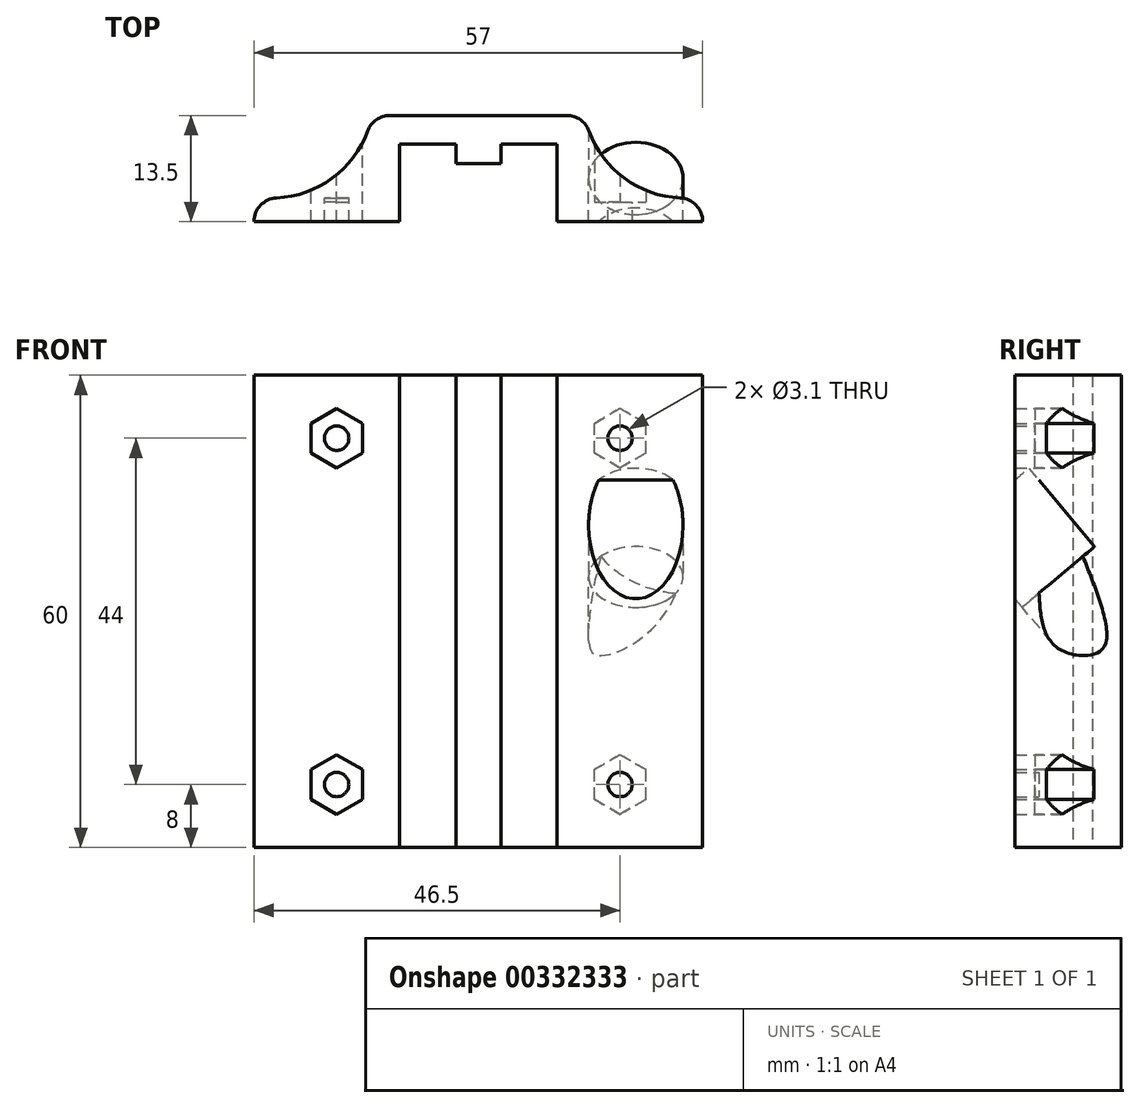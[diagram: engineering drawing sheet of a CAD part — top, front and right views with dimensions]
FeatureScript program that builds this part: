
annotation { "Feature Type Name" : "Feature", "Feature Type Description" : "" }
export const myFeature = defineFeature(function(context is Context, id is Id, definition is map)
    precondition{}
    {
        {
            var Q0;
            Q0=qCreatedBy(makeId("Top.planeOp"),FACE);
            var sketch = newSketch(context, id + "F0", { "sketchPlane" : qUnion([Q0])});
            skLineSegment(sketch, "E0.bottom", {"start": v(10, -9.85) * mm, "end": v(-10, -9.85) * mm});
            skLineSegment(sketch, "E0.top", {"start": v(10, 9.85) * mm, "end": v(-10, 9.85) * mm});
            skLineSegment(sketch, "E0.left", {"start": v(10, -9.85) * mm, "end": v(10, 9.85) * mm});
            skLineSegment(sketch, "E0.right", {"start": v(-10, -9.85) * mm, "end": v(-10, 9.85) * mm});
            skPoint(sketch, "E0.middle", {"position": v(0, 0) * mm});
            skLineSegment(sketch, "E1.left", {"start": v(2.85, 9.85) * mm, "end": v(2.85, 7.35) * mm});
            skLineSegment(sketch, "E1.right", {"start": v(-2.85, 9.85) * mm, "end": v(-2.85, 7.35) * mm});
            skLineSegment(sketch, "E2.bottom", {"start": v(10, -3) * mm, "end": v(6, -3) * mm});
            skLineSegment(sketch, "E2.top", {"start": v(10, 3) * mm, "end": v(6, 3) * mm});
            skLineSegment(sketch, "E3.0", {"start": v(2.85, 7.35) * mm, "end": v(-2.85, 7.35) * mm});
            skLineSegment(sketch, "E4.0", {"start": v(6, -3) * mm, "end": v(6, 3) * mm});
            skLineSegment(sketch, "E5.MirrorCS", {"start": v(-10, 3) * mm, "end": v(-6, 3) * mm});
            skLineSegment(sketch, "E6.MirrorCS", {"start": v(-6, -3) * mm, "end": v(-6, 3) * mm});
            skLineSegment(sketch, "E7.MirrorCS", {"start": v(-10, -3) * mm, "end": v(-6, -3) * mm});
            skLineSegment(sketch, "E8.MirrorCS", {"start": v(-2.85, -9.85) * mm, "end": v(-2.85, -7.35) * mm});
            skLineSegment(sketch, "E9.MirrorCS", {"start": v(2.85, -7.35) * mm, "end": v(-2.85, -7.35) * mm});
            skLineSegment(sketch, "E10.MirrorCS", {"start": v(2.85, -9.85) * mm, "end": v(2.85, -7.35) * mm});
            skLineSegment(sketch, "E11.bottom", {"start": v(13.5, -13.5) * mm, "end": v(-13.5, -13.5) * mm});
            skLineSegment(sketch, "E11.top", {"start": v(13.5, 13.5) * mm, "end": v(-13.5, 13.5) * mm});
            skLineSegment(sketch, "E11.left", {"start": v(13.5, -13.5) * mm, "end": v(13.5, 13.5) * mm});
            skLineSegment(sketch, "E11.right", {"start": v(-13.5, -13.5) * mm, "end": v(-13.5, 13.5) * mm});
            skLineSegment(sketch, "E12.bottom", {"start": v(28.5, -3) * mm, "end": v(13.5, -3) * mm});
            skLineSegment(sketch, "E12.top", {"start": v(28.5, 3) * mm, "end": v(13.5, 3) * mm});
            skLineSegment(sketch, "E12.left", {"start": v(28.5, -3) * mm, "end": v(28.5, 3) * mm});
            skLineSegment(sketch, "E12.right", {"start": v(13.5, -3) * mm, "end": v(13.5, 3) * mm});
            skPoint(sketch, "E12.middle", {"position": v(21, 0) * mm});
            skLineSegment(sketch, "E13.MirrorCS", {"start": v(-28.5, 3) * mm, "end": v(-13.5, 3) * mm});
            skLineSegment(sketch, "E14.MirrorCS", {"start": v(-28.5, -3) * mm, "end": v(-28.5, 3) * mm});
            skLineSegment(sketch, "E15.MirrorCS", {"start": v(-28.5, -3) * mm, "end": v(-13.5, -3) * mm});
            skLineSegment(sketch, "E16", {"start": v(-28.5, 0) * mm, "end": v(28.5, 0) * mm});
            skSolve(sketch);
        }
        {
            var Q0;
            {var subQ0=sQuery(id+"F0.wireOp",EDGE,"E13.MirrorCS");Q0=makeQuery(id+"F0.imprint","IMPRINT",FACE,{"disambiguationData":[TD([[makeQuery(id+"F0.imprint","IMPRINT",EDGE,{"derivedFrom":subQ0}),-1.0]])]});}
            var Q1;
            {var subQ0=sQuery(id+"F0.wireOp",EDGE,"E11.top");Q1=makeQuery(id+"F0.imprint","IMPRINT",FACE,{"disambiguationData":[TD([[makeQuery(id+"F0.imprint","IMPRINT",EDGE,{"derivedFrom":subQ0}),1.0]])]});}
            var Q2;
            {var subQ0=sQuery(id+"F0.wireOp",EDGE,"E1.left");Q2=makeQuery(id+"F0.imprint","IMPRINT",FACE,{"disambiguationData":[TD([[makeQuery(id+"F0.imprint","IMPRINT",EDGE,{"derivedFrom":subQ0}),-1.0]])]});}
            var Q3;
            {var subQ0=sQuery(id+"F0.wireOp",EDGE,"E12.top");Q3=makeQuery(id+"F0.imprint","IMPRINT",FACE,{"disambiguationData":[TD([[makeQuery(id+"F0.imprint","IMPRINT",EDGE,{"derivedFrom":subQ0}),1.0]])]});}
            extrude(context, id + "F1", {"entities" : qUnion([Q0, Q1, Q2, Q3]), "depth" : 60 * mm});
        }
        {
            var Q0;
            {var subQ0=sQuery(id+"F0.wireOp",EDGE,"E15.MirrorCS");Q0=makeQuery(id+"F0.imprint","IMPRINT",FACE,{"disambiguationData":[TD([[makeQuery(id+"F0.imprint","IMPRINT",EDGE,{"derivedFrom":subQ0}),1.0]])]});}
            var Q1;
            {var subQ1=sQuery(id+"F0.wireOp",EDGE,"E11.bottom");Q1=makeQuery(id+"F0.imprint","IMPRINT",FACE,{"disambiguationData":[TD([[makeQuery(id+"F0.imprint","IMPRINT",EDGE,{"derivedFrom":subQ1}),-1.0]])]});}
            var Q2;
            {var subQ0=sQuery(id+"F0.wireOp",EDGE,"E8.MirrorCS");Q2=makeQuery(id+"F0.imprint","IMPRINT",FACE,{"disambiguationData":[TD([[makeQuery(id+"F0.imprint","IMPRINT",EDGE,{"derivedFrom":subQ0}),-1.0]])]});}
            var Q3;
            {var subQ0=sQuery(id+"F0.wireOp",EDGE,"E12.bottom");Q3=makeQuery(id+"F0.imprint","IMPRINT",FACE,{"disambiguationData":[TD([[makeQuery(id+"F0.imprint","IMPRINT",EDGE,{"derivedFrom":subQ0}),-1.0]])]});}
            extrude(context, id + "F2", {"entities" : qUnion([Q0, Q1, Q2, Q3]), "depth" : 60 * mm});
        }
        {
            var Q0;
            Q0=qCreatedBy(makeId("Front.planeOp"),FACE);
            var sketch = newSketch(context, id + "F3", { "sketchPlane" : qUnion([Q0])});
            skCircle(sketch, "E17", {"center": v(18, 52) * mm, "radius": 1.55 * mm});
            skCircle(sketch, "E18", {"center": v(18, 8) * mm, "radius": 1.55 * mm});
            skCircle(sketch, "E19.cCircle", {"center": v(18, 52) * mm, "radius": 3.28 * mm, "construction": true});
            skLineSegment(sketch, "E19.0", {"start": v(21.27, 53.9) * mm, "end": v(21.27, 50.1) * mm});
            skLineSegment(sketch, "E19.1", {"start": v(21.27, 50.1) * mm, "end": v(18, 48.22) * mm});
            skLineSegment(sketch, "E19.2", {"start": v(18, 48.22) * mm, "end": v(14.72, 50.1) * mm});
            skLineSegment(sketch, "E19.3", {"start": v(14.72, 50.1) * mm, "end": v(14.72, 53.9) * mm});
            skLineSegment(sketch, "E19.4", {"start": v(14.72, 53.9) * mm, "end": v(18, 55.78) * mm});
            skLineSegment(sketch, "E19.5", {"start": v(18, 55.78) * mm, "end": v(21.27, 53.9) * mm});
            skPoint(sketch, "E19.0.midPoint", {"position": v(21.27, 52) * mm});
            skCircle(sketch, "E20.cCircle", {"center": v(18, 8) * mm, "radius": 3.28 * mm, "construction": true});
            skLineSegment(sketch, "E20.0", {"start": v(21.28, 9.9) * mm, "end": v(21.28, 6.1) * mm});
            skLineSegment(sketch, "E20.1", {"start": v(21.28, 6.1) * mm, "end": v(18, 4.22) * mm});
            skLineSegment(sketch, "E20.2", {"start": v(18, 4.22) * mm, "end": v(14.73, 6.1) * mm});
            skLineSegment(sketch, "E20.3", {"start": v(14.73, 6.1) * mm, "end": v(14.73, 9.9) * mm});
            skLineSegment(sketch, "E20.4", {"start": v(14.73, 9.9) * mm, "end": v(18, 11.78) * mm});
            skLineSegment(sketch, "E20.5", {"start": v(18, 11.78) * mm, "end": v(21.28, 9.9) * mm});
            skPoint(sketch, "E20.0.midPoint", {"position": v(21.28, 8) * mm});
            skPoint(sketch, "E21.MirrorP", {"position": v(-21.27, 52) * mm});
            skCircle(sketch, "E22.MirrorC", {"center": v(-18, 52) * mm, "radius": 1.55 * mm});
            skLineSegment(sketch, "E23.MirrorCS", {"start": v(-18, 55.78) * mm, "end": v(-21.27, 53.9) * mm});
            skLineSegment(sketch, "E24.MirrorCS", {"start": v(-14.72, 53.9) * mm, "end": v(-18, 55.78) * mm});
            skLineSegment(sketch, "E25.MirrorCS", {"start": v(-14.72, 50.1) * mm, "end": v(-14.72, 53.9) * mm});
            skLineSegment(sketch, "E26.MirrorCS", {"start": v(-18, 48.22) * mm, "end": v(-14.72, 50.1) * mm});
            skLineSegment(sketch, "E27.MirrorCS", {"start": v(-21.27, 50.1) * mm, "end": v(-18, 48.22) * mm});
            skCircle(sketch, "E28.MirrorC", {"center": v(-18, 52) * mm, "radius": 3.28 * mm, "construction": true});
            skLineSegment(sketch, "E29.MirrorCS", {"start": v(-21.27, 53.9) * mm, "end": v(-21.27, 50.1) * mm});
            skLineSegment(sketch, "E30.MirrorCS", {"start": v(-21.28, 9.9) * mm, "end": v(-21.28, 6.1) * mm});
            skLineSegment(sketch, "E31.MirrorCS", {"start": v(-18, 11.78) * mm, "end": v(-21.28, 9.9) * mm});
            skPoint(sketch, "E32.MirrorP", {"position": v(-21.28, 8) * mm});
            skLineSegment(sketch, "E33.MirrorCS", {"start": v(-14.73, 9.9) * mm, "end": v(-18, 11.78) * mm});
            skLineSegment(sketch, "E34.MirrorCS", {"start": v(-14.73, 6.1) * mm, "end": v(-14.73, 9.9) * mm});
            skCircle(sketch, "E35.MirrorC", {"center": v(-18, 8) * mm, "radius": 1.55 * mm});
            skCircle(sketch, "E36.MirrorC", {"center": v(-18, 8) * mm, "radius": 3.28 * mm, "construction": true});
            skLineSegment(sketch, "E37.MirrorCS", {"start": v(-18, 4.22) * mm, "end": v(-14.73, 6.1) * mm});
            skLineSegment(sketch, "E38.MirrorCS", {"start": v(-21.28, 6.1) * mm, "end": v(-18, 4.22) * mm});
            skSolve(sketch);
        }
        {
            var Q0;
            Q0=makeQuery(id+"F3.imprint","IMPRINT",FACE,{"disambiguationData":[TD([[makeQuery(id+"F3.imprint","IMPRINT",EDGE,{"derivedFrom":sQuery(id+"F3.wireOp",EDGE,"E17")}),1.0]])]});
            var Q1;
            Q1=makeQuery(id+"F3.imprint","IMPRINT",FACE,{"disambiguationData":[TD([[makeQuery(id+"F3.imprint","IMPRINT",EDGE,{"derivedFrom":sQuery(id+"F3.wireOp",EDGE,"E22.MirrorC")}),-1.0]])]});
            var Q2;
            Q2=makeQuery(id+"F3.imprint","IMPRINT",FACE,{"disambiguationData":[TD([[makeQuery(id+"F3.imprint","IMPRINT",EDGE,{"derivedFrom":sQuery(id+"F3.wireOp",EDGE,"E35.MirrorC")}),-1.0]])]});
            var Q3;
            Q3=makeQuery(id+"F3.imprint","IMPRINT",FACE,{"disambiguationData":[TD([[makeQuery(id+"F3.imprint","IMPRINT",EDGE,{"derivedFrom":sQuery(id+"F3.wireOp",EDGE,"E18")}),1.0]])]});
            extrude(context, id + "F4", {"entities" : qUnion([Q0, Q1, Q2, Q3]), "operationType" : NewBodyOperationType.REMOVE, "depth" : 10 * mm, "hasSecondDirection" : true, "secondDirectionOppositeDirection" : true, "secondDirectionDepth" : 10 * mm});
        }
        {
            var Q0;
            Q0=makeQuery(id+"F1.opExtrude","SWEPT_EDGE",EDGE,{"disambiguationData":[OSD([sQuery(id+"F0.wireOp",EDGE,"E11.left"),sQuery(id+"F0.wireOp",EDGE,"E12.top"),sQuery(id+"F0.wireOp",EDGE,"E12.right")])]});
            var Q1;
            Q1=makeQuery(id+"F1.opExtrude","SWEPT_EDGE",EDGE,{"disambiguationData":[OSD([sQuery(id+"F0.wireOp",EDGE,"E11.right"),sQuery(id+"F0.wireOp",EDGE,"E13.MirrorCS")])]});
            var Q2;
            Q2=makeQuery(id+"F2.opExtrude","SWEPT_EDGE",EDGE,{"disambiguationData":[OSD([sQuery(id+"F0.wireOp",EDGE,"E11.right"),sQuery(id+"F0.wireOp",EDGE,"E15.MirrorCS")])]});
            var Q3;
            Q3=makeQuery(id+"F2.opExtrude","SWEPT_EDGE",EDGE,{"disambiguationData":[OSD([sQuery(id+"F0.wireOp",EDGE,"E11.left"),sQuery(id+"F0.wireOp",EDGE,"E12.bottom"),sQuery(id+"F0.wireOp",EDGE,"E12.right")])]});
            fillet(context, id + "F5", {"entities" : qUnion([Q0, Q1, Q2, Q3]), "radius" : 13 * mm, "tangentPropagation" : true, "allowEdgeOverflow" : false});
        }
        {
            var Q0;
            Q0=qCreatedBy(makeId("Front.planeOp"),FACE);
            var sketch = newSketch(context, id + "F6", { "sketchPlane" : qUnion([Q0])});
            skCircle(sketch, "E39", {"center": v(18, 52) * mm, "radius": 2.6 * mm});
            skCircle(sketch, "E40", {"center": v(18, 8) * mm, "radius": 2.6 * mm});
            skCircle(sketch, "E41", {"center": v(-18, 52) * mm, "radius": 2.6 * mm});
            skCircle(sketch, "E42", {"center": v(-18, 8) * mm, "radius": 2.6 * mm});
            skSolve(sketch);
        }
        {
            var Q0;
            Q0=makeQuery(id+"F6.imprint","IMPRINT",FACE,{"disambiguationData":[TD([[makeQuery(id+"F6.imprint","IMPRINT",EDGE,{"derivedFrom":sQuery(id+"F6.wireOp",EDGE,"E39")}),1.0]])]});
            var Q1;
            Q1=makeQuery(id+"F3.imprint","IMPRINT",FACE,{"disambiguationData":[TD([[makeQuery(id+"F3.imprint","IMPRINT",EDGE,{"derivedFrom":sQuery(id+"F3.wireOp",EDGE,"E17")}),1.0]])]});
            var Q2;
            Q2=makeQuery(id+"F6.imprint","IMPRINT",FACE,{"disambiguationData":[TD([[makeQuery(id+"F6.imprint","IMPRINT",EDGE,{"derivedFrom":sQuery(id+"F6.wireOp",EDGE,"E40")}),1.0]])]});
            var Q3;
            Q3=makeQuery(id+"F3.imprint","IMPRINT",FACE,{"disambiguationData":[TD([[makeQuery(id+"F3.imprint","IMPRINT",EDGE,{"derivedFrom":sQuery(id+"F3.wireOp",EDGE,"E18")}),1.0]])]});
            var Q4;
            Q4=makeQuery(id+"F6.imprint","IMPRINT",FACE,{"disambiguationData":[TD([[makeQuery(id+"F6.imprint","IMPRINT",EDGE,{"derivedFrom":sQuery(id+"F6.wireOp",EDGE,"E42")}),1.0]])]});
            var Q5;
            Q5=makeQuery(id+"F3.imprint","IMPRINT",FACE,{"disambiguationData":[TD([[makeQuery(id+"F3.imprint","IMPRINT",EDGE,{"derivedFrom":sQuery(id+"F3.wireOp",EDGE,"E35.MirrorC")}),-1.0]])]});
            var Q6;
            Q6=makeQuery(id+"F6.imprint","IMPRINT",FACE,{"disambiguationData":[TD([[makeQuery(id+"F6.imprint","IMPRINT",EDGE,{"derivedFrom":sQuery(id+"F6.wireOp",EDGE,"E41")}),1.0]])]});
            var Q7;
            Q7=makeQuery(id+"F3.imprint","IMPRINT",FACE,{"disambiguationData":[TD([[makeQuery(id+"F3.imprint","IMPRINT",EDGE,{"derivedFrom":sQuery(id+"F3.wireOp",EDGE,"E22.MirrorC")}),-1.0]])]});
            extrude(context, id + "F7", {"entities" : qUnion([Q0, Q1, Q2, Q3, Q4, Q5, Q6, Q7]), "operationType" : NewBodyOperationType.REMOVE, "depth" : 25 * mm, "hasSecondDirection" : true, "secondDirectionOppositeDirection" : false, "secondDirectionDepth" : 3 * mm});
        }
        {
            var Q0;
            {var subQ3=sQuery(id+"F0.wireOp",EDGE,"E1.left");Q0=makeQuery(id+"F0.imprint","IMPRINT",FACE,{"disambiguationData":[TD([[makeQuery(id+"F0.imprint","IMPRINT",EDGE,{"derivedFrom":subQ3}),1.0]])]});}
            var Q1;
            {var subQ0=sQuery(id+"F0.wireOp",EDGE,"E2.top");Q1=makeQuery(id+"F0.imprint","IMPRINT",FACE,{"disambiguationData":[TD([[makeQuery(id+"F0.imprint","IMPRINT",EDGE,{"derivedFrom":subQ0}),1.0]])]});}
            var Q2;
            {var subQ0=sQuery(id+"F0.wireOp",EDGE,"E5.MirrorCS");Q2=makeQuery(id+"F0.imprint","IMPRINT",FACE,{"disambiguationData":[TD([[makeQuery(id+"F0.imprint","IMPRINT",EDGE,{"derivedFrom":subQ0}),-1.0]])]});}
            extrude(context, id + "F8", {"entities" : qUnion([Q0, Q1, Q2]), "operationType" : NewBodyOperationType.REMOVE, "depth" : 40 * mm});
        }
        {
            var Q0;
            Q0=makeQuery(id+"F5.opFillet","BLEND_EDGE",EDGE,{"blendedFrom":[makeQuery(id+"F2.opExtrude","SWEPT_EDGE",EDGE,{"disambiguationData":[OSD([sQuery(id+"F0.wireOp",EDGE,"E11.left"),sQuery(id+"F0.wireOp",EDGE,"E12.bottom"),sQuery(id+"F0.wireOp",EDGE,"E12.right")])]}),makeQuery(id+"F2.opExtrude","SWEPT_FACE",FACE,{"disambiguationData":[OSD([sQuery(id+"F0.wireOp",EDGE,"E11.bottom")])]})],"blendedInto":[makeQuery(id+"F2.opExtrude","SWEPT_FACE",FACE,{"disambiguationData":[OSD([sQuery(id+"F0.wireOp",EDGE,"E11.bottom")])]})]});
            var Q1;
            Q1=makeQuery(id+"F5.opFillet","BLEND_EDGE",EDGE,{"blendedFrom":[makeQuery(id+"F2.opExtrude","SWEPT_EDGE",EDGE,{"disambiguationData":[OSD([sQuery(id+"F0.wireOp",EDGE,"E11.right"),sQuery(id+"F0.wireOp",EDGE,"E15.MirrorCS")])]}),makeQuery(id+"F2.opExtrude","SWEPT_FACE",FACE,{"disambiguationData":[OSD([sQuery(id+"F0.wireOp",EDGE,"E11.bottom")])]})],"blendedInto":[makeQuery(id+"F2.opExtrude","SWEPT_FACE",FACE,{"disambiguationData":[OSD([sQuery(id+"F0.wireOp",EDGE,"E11.bottom")])]})]});
            var Q2;
            Q2=makeQuery(id+"F5.opFillet","BLEND_EDGE",EDGE,{"blendedFrom":[makeQuery(id+"F1.opExtrude","SWEPT_EDGE",EDGE,{"disambiguationData":[OSD([sQuery(id+"F0.wireOp",EDGE,"E11.left"),sQuery(id+"F0.wireOp",EDGE,"E12.top"),sQuery(id+"F0.wireOp",EDGE,"E12.right")])]}),makeQuery(id+"F1.opExtrude","SWEPT_FACE",FACE,{"disambiguationData":[OSD([sQuery(id+"F0.wireOp",EDGE,"E11.top")])]})],"blendedInto":[makeQuery(id+"F1.opExtrude","SWEPT_FACE",FACE,{"disambiguationData":[OSD([sQuery(id+"F0.wireOp",EDGE,"E11.top")])]})]});
            var Q3;
            Q3=makeQuery(id+"F5.opFillet","BLEND_EDGE",EDGE,{"blendedFrom":[makeQuery(id+"F1.opExtrude","SWEPT_EDGE",EDGE,{"disambiguationData":[OSD([sQuery(id+"F0.wireOp",EDGE,"E11.right"),sQuery(id+"F0.wireOp",EDGE,"E13.MirrorCS")])]}),makeQuery(id+"F1.opExtrude","SWEPT_FACE",FACE,{"disambiguationData":[OSD([sQuery(id+"F0.wireOp",EDGE,"E11.top")])]})],"blendedInto":[makeQuery(id+"F1.opExtrude","SWEPT_FACE",FACE,{"disambiguationData":[OSD([sQuery(id+"F0.wireOp",EDGE,"E11.top")])]})]});
            fillet(context, id + "F9", {"entities" : qUnion([Q0, Q1, Q2, Q3]), "radius" : 3 * mm, "tangentPropagation" : true, "allowEdgeOverflow" : false});
        }
        {
            var Q0;
            Q0=qCreatedBy(makeId("Front.planeOp"),FACE);
            var sketch = newSketch(context, id + "F10", { "sketchPlane" : qUnion([Q0])});
            skLineSegment(sketch, "E43.bottom", {"start": v(-10, 15) * mm, "end": v(-4, 15) * mm});
            skLineSegment(sketch, "E43.top", {"start": v(-10, 45) * mm, "end": v(-4, 45) * mm});
            skLineSegment(sketch, "E43.left", {"start": v(-10, 15) * mm, "end": v(-10, 45) * mm});
            skLineSegment(sketch, "E43.right", {"start": v(-4, 15) * mm, "end": v(-4, 45) * mm});
            skPoint(sketch, "E43.middle", {"position": v(0, 31.47) * mm});
            skSolve(sketch);
        }
        {
            var Q0;
            Q0=makeQuery(id+"F10.imprint","IMPRINT",FACE,{"disambiguationData":[TD([[makeQuery(id+"F10.imprint","IMPRINT",EDGE,{"derivedFrom":sQuery(id+"F10.wireOp",EDGE,"E43.bottom")}),1.0]])]});
            extrude(context, id + "F11", {"entities" : qUnion([Q0]), "operationType" : NewBodyOperationType.ADD, "depth" : 26 * mm, "hasSecondDirection" : true, "secondDirectionOppositeDirection" : false, "secondDirectionDepth" : 11 * mm});
        }
        {
            var Q0;
            {var subQ1=sQuery(id+"F10.wireOp",EDGE,"E43.left");Q0=makeQuery(id+"F11.boolean.opBoolean","SPLIT",FACE,{"disambiguationData":[TD([makeQuery(id+"FrOpPQLDhbuZp0P_2.opFillet","BLEND_FACE",FACE,{"disambiguationData":[OSD([sQuery(id+"F0.wireOp",EDGE,"E11.bottom"),sQuery(id+"F0.wireOp",EDGE,"E11.right")])]})])],"derivedFrom":makeQuery(id+"F11.opExtrude","SWEPT_FACE",FACE,{"disambiguationData":[OSD([subQ1])]})});}
            cPlane(context, id + "F12", {"entities" : qUnion([Q0]), "cplaneType" : CPlaneType.OFFSET, "offset" : 0 * mm, "width" : 150 * mm, "height" : 150 * mm});
        }
        {
            var Q0;
            Q0=qCreatedBy(id+"F12.planeOp",FACE);
            var sketch = newSketch(context, id + "F13", { "sketchPlane" : qUnion([Q0])});
            skCircle(sketch, "E44", {"center": v(21, 30) * mm, "radius": 1.55 * mm});
            skCircle(sketch, "E45.cCircle", {"center": v(21, 30) * mm, "radius": 3.28 * mm, "construction": true});
            skLineSegment(sketch, "E45.0", {"start": v(24.28, 31.9) * mm, "end": v(24.28, 28.1) * mm});
            skLineSegment(sketch, "E45.1", {"start": v(24.28, 28.1) * mm, "end": v(21, 26.22) * mm});
            skLineSegment(sketch, "E45.2", {"start": v(21, 26.22) * mm, "end": v(17.72, 28.1) * mm});
            skLineSegment(sketch, "E45.3", {"start": v(17.73, 28.1) * mm, "end": v(17.73, 31.9) * mm});
            skLineSegment(sketch, "E45.4", {"start": v(17.73, 31.9) * mm, "end": v(21, 33.78) * mm});
            skLineSegment(sketch, "E45.5", {"start": v(21, 33.78) * mm, "end": v(24.28, 31.9) * mm});
            skPoint(sketch, "E45.0.midPoint", {"position": v(24.28, 30) * mm});
            skSolve(sketch);
        }
        {
            var Q0;
            Q0=makeQuery(id+"F11.boolean.opBoolean","INTERSECT",EDGE,{"derivedFrom":[makeQuery(id+"FrOpPQLDhbuZp0P_2.opFillet","BLEND_FACE",FACE,{"disambiguationData":[OSD([sQuery(id+"F0.wireOp",EDGE,"E11.bottom"),sQuery(id+"F0.wireOp",EDGE,"E11.right")])]}),makeQuery(id+"F11.opExtrude","SWEPT_FACE",FACE,{"disambiguationData":[OSD([sQuery(id+"F10.wireOp",EDGE,"E43.left")])]})]});
            var Q1;
            Q1=makeQuery(id+"F11.boolean.opBoolean","INTERSECT",EDGE,{"derivedFrom":[makeQuery(id+"FrOpPQLDhbuZp0P_2.opFillet","BLEND_FACE",FACE,{"disambiguationData":[OSD([sQuery(id+"F0.wireOp",EDGE,"E11.bottom"),sQuery(id+"F0.wireOp",EDGE,"E11.right")])]}),makeQuery(id+"F11.opExtrude","SWEPT_FACE",FACE,{"disambiguationData":[OSD([sQuery(id+"F10.wireOp",EDGE,"E43.top")])]})]});
            var Q2;
            Q2=makeQuery(id+"F11.boolean.opBoolean","INTERSECT",EDGE,{"derivedFrom":[makeQuery(id+"FrOpPQLDhbuZp0P_2.opFillet","BLEND_FACE",FACE,{"disambiguationData":[OSD([sQuery(id+"F0.wireOp",EDGE,"E11.bottom"),sQuery(id+"F0.wireOp",EDGE,"E11.right")])]}),makeQuery(id+"F11.opExtrude","SWEPT_FACE",FACE,{"disambiguationData":[OSD([sQuery(id+"F10.wireOp",EDGE,"E43.bottom")])]})]});
            var Q3;
            Q3=makeQuery(id+"F11.boolean.opBoolean","INTERSECT",EDGE,{"derivedFrom":[makeQuery(id+"F2.opExtrude","SWEPT_FACE",FACE,{"disambiguationData":[OSD([sQuery(id+"F0.wireOp",EDGE,"E11.bottom")])]}),makeQuery(id+"F11.opExtrude","SWEPT_FACE",FACE,{"disambiguationData":[OSD([sQuery(id+"F10.wireOp",EDGE,"E43.right")])]})]});
            fillet(context, id + "F14", {"entities" : qUnion([Q0, Q1, Q2, Q3]), "radius" : 2 * mm, "tangentPropagation" : true, "allowEdgeOverflow" : false});
        }
        {
            var Q0;
            Q0=makeQuery(id+"F11.opExtrude","CAP_EDGE",EDGE,{"disambiguationData":[OSD([sQuery(id+"F10.wireOp",EDGE,"E43.top")])],"isStart":false});
            var Q1;
            Q1=makeQuery(id+"F11.opExtrude","CAP_EDGE",EDGE,{"disambiguationData":[OSD([sQuery(id+"F10.wireOp",EDGE,"E43.bottom")])],"isStart":false});
            fillet(context, id + "F15", {"entities" : qUnion([Q0, Q1]), "radius" : 5 * mm, "tangentPropagation" : true, "allowEdgeOverflow" : false});
        }
        {
            var Q0;
            Q0=makeQuery(id+"F11.opExtrude","CAP_EDGE",EDGE,{"disambiguationData":[OSD([sQuery(id+"F10.wireOp",EDGE,"E43.left")])],"isStart":false});
            var Q1;
            {var subQ0=makeQuery(id+"FrOpPQLDhbuZp0P_2.opFillet","BLEND_FACE",FACE,{"disambiguationData":[OSD([sQuery(id+"F0.wireOp",EDGE,"E11.bottom"),sQuery(id+"F0.wireOp",EDGE,"E11.right")])]});Q1=makeQuery(id+"F14.opFillet","BLEND_EDGE",EDGE,{"disambiguationData":[OD(1.0)],"blendedFrom":[makeQuery(id+"F11.boolean.opBoolean","INTERSECT",EDGE,{"derivedFrom":[subQ0,makeQuery(id+"F11.opExtrude","SWEPT_FACE",FACE,{"disambiguationData":[OSD([sQuery(id+"F10.wireOp",EDGE,"E43.top")])]})]}),makeQuery(id+"F11.boolean.opBoolean","INTERSECT",EDGE,{"derivedFrom":[subQ0,makeQuery(id+"F11.opExtrude","SWEPT_FACE",FACE,{"disambiguationData":[OSD([sQuery(id+"F10.wireOp",EDGE,"E43.left")])]})]})],"blendedInto":[]});}
            var Q2;
            {var subQ0=makeQuery(id+"FrOpPQLDhbuZp0P_2.opFillet","BLEND_FACE",FACE,{"disambiguationData":[OSD([sQuery(id+"F0.wireOp",EDGE,"E11.bottom"),sQuery(id+"F0.wireOp",EDGE,"E11.right")])]});Q2=makeQuery(id+"F14.opFillet","BLEND_EDGE",EDGE,{"disambiguationData":[OD(1.0)],"blendedFrom":[makeQuery(id+"F11.boolean.opBoolean","INTERSECT",EDGE,{"derivedFrom":[subQ0,makeQuery(id+"F11.opExtrude","SWEPT_FACE",FACE,{"disambiguationData":[OSD([sQuery(id+"F10.wireOp",EDGE,"E43.bottom")])]})]}),makeQuery(id+"F11.boolean.opBoolean","INTERSECT",EDGE,{"derivedFrom":[subQ0,makeQuery(id+"F11.opExtrude","SWEPT_FACE",FACE,{"disambiguationData":[OSD([sQuery(id+"F10.wireOp",EDGE,"E43.left")])]})]})],"blendedInto":[]});}
            var Q3;
            Q3=makeQuery(id+"F11.opExtrude","SWEPT_EDGE",EDGE,{"disambiguationData":[OSD([sQuery(id+"F10.wireOp",EDGE,"E43.bottom"),sQuery(id+"F10.wireOp",EDGE,"E43.left")])]});
            fillet(context, id + "F16", {"entities" : qUnion([Q0, Q1, Q2, Q3]), "radius" : 4 * mm, "tangentPropagation" : true, "allowEdgeOverflow" : false});
        }
        {
            var Q0;
            Q0=makeQuery(id+"F13.imprint","IMPRINT",FACE,{"disambiguationData":[TD([[makeQuery(id+"F13.imprint","IMPRINT",EDGE,{"derivedFrom":sQuery(id+"F13.wireOp",EDGE,"E44")}),1.0]])]});
            extrude(context, id + "F17", {"entities" : qUnion([Q0]), "operationType" : NewBodyOperationType.REMOVE, "oppositeDirection" : true, "depth" : 25 * mm});
        }
        {
            var Q0;
            Q0=makeQuery(id+"F13.imprint","IMPRINT",FACE,{"disambiguationData":[TD([[makeQuery(id+"F13.imprint","IMPRINT",EDGE,{"derivedFrom":sQuery(id+"F13.wireOp",EDGE,"E44")}),-1.0]])]});
            extrude(context, id + "F18", {"entities" : qUnion([Q0]), "operationType" : NewBodyOperationType.REMOVE, "oppositeDirection" : true, "depth" : 2.5 * mm});
        }
        {
            var Q0;
            Q0=qCreatedBy(makeId("Front.planeOp"),FACE);
            cPlane(context, id + "F19", {"entities" : qUnion([Q0]), "cplaneType" : CPlaneType.OFFSET, "offset" : 10 * mm, "oppositeDirection" : true, "width" : 150 * mm, "height" : 150 * mm});
        }
        {
            var Q0;
            Q0=qCreatedBy(id+"F19.planeOp",FACE);
            var sketch = newSketch(context, id + "F20", { "sketchPlane" : qUnion([Q0])});
            skPoint(sketch, "E46.middle", {"position": v(0, 30) * mm});
            skCircle(sketch, "E47", {"center": v(20, 30) * mm, "radius": 6 * mm});
            skCircle(sketch, "E48.MirrorC", {"center": v(-20, 30) * mm, "radius": 6 * mm});
            skSolve(sketch);
        }
        {
            var Q0;
            Q0=qCreatedBy(makeId("Right.planeOp"),FACE);
            var sketch = newSketch(context, id + "F21", { "sketchPlane" : qUnion([Q0])});
            skCircle(sketch, "E49", {"center": v(10, 30) * mm, "radius": 3 * mm});
            skSolve(sketch);
        }
        {
            var Q0;
            Q0=makeQuery(id+"F20.imprint","IMPRINT",FACE,{"disambiguationData":[TD([[makeQuery(id+"F20.imprint","IMPRINT",EDGE,{"derivedFrom":sQuery(id+"F20.wireOp",EDGE,"E47")}),1.0]])]});
            var Q1;
            Q1=makeQuery(id+"F20.imprint","IMPRINT",FACE,{"disambiguationData":[TD([[makeQuery(id+"F20.imprint","IMPRINT",EDGE,{"derivedFrom":sQuery(id+"F20.wireOp",EDGE,"E48.MirrorC")}),-1.0]])]});
            extrude(context, id + "F22", {"entities" : qUnion([Q0, Q1]), "depth" : 20 * mm, "hasSecondDirection" : true, "secondDirectionOppositeDirection" : false, "secondDirectionDepth" : 7 * mm});
        }
        {
            var Q0;
            Q0=makeQuery(id+"F22.opExtrude","SWEPT_BODY",BODY,{"disambiguationData":[OSD([sQuery(id+"F20.wireOp",EDGE,"E47")])]});
            var Q1;
            Q1=makeQuery(id+"F22.opExtrude","SWEPT_BODY",BODY,{"disambiguationData":[OSD([sQuery(id+"F20.wireOp",EDGE,"E48.MirrorC")])]});
            var Q2;
            Q2=sQuery(id+"F21.wireOp",EDGE,"E49");
            transform(context, id + "F23", {"entities" : qUnion([Q0, Q1]), "transformType" : TransformType.ROTATION, "transformAxis" : qUnion([Q2]), "angle" : 50 * degree, "oppositeDirection" : true, "makeCopy" : false});
        }
        {
            var Q0;
            Q0=makeQuery(id+"F22.opExtrude","SWEPT_BODY",BODY,{"disambiguationData":[OSD([sQuery(id+"F20.wireOp",EDGE,"E47")])]});
            var Q1;
            Q1=makeQuery(id+"F22.opExtrude","SWEPT_BODY",BODY,{"disambiguationData":[OSD([sQuery(id+"F20.wireOp",EDGE,"E48.MirrorC")])]});
            transform(context, id + "F24", {"entities" : qUnion([Q0, Q1]), "transformType" : TransformType.TRANSLATION_3D, "dx" : 0 * mm, "dy" : 0 * mm, "dz" : -1 * mm, "makeCopy" : false});
        }
        {
            var Q0;
            Q0=qCreatedBy(makeId("Right.planeOp"),FACE);
            var sketch = newSketch(context, id + "F25", { "sketchPlane" : qUnion([Q0])});
            skLineSegment(sketch, "E50.bottom", {"start": v(-39.19, 0) * mm, "end": v(0, 0) * mm});
            skLineSegment(sketch, "E50.top", {"start": v(-39.19, 69.98) * mm, "end": v(0, 69.98) * mm});
            skLineSegment(sketch, "E50.left", {"start": v(-39.19, 0) * mm, "end": v(-39.19, 69.98) * mm});
            skLineSegment(sketch, "E50.right", {"start": v(0, 0) * mm, "end": v(0, 69.98) * mm});
            skSolve(sketch);
        }
        {
            var Q0;
            Q0=makeQuery(id+"F25.imprint","IMPRINT",FACE,{"disambiguationData":[TD([[makeQuery(id+"F25.imprint","IMPRINT",EDGE,{"derivedFrom":sQuery(id+"F25.wireOp",EDGE,"E50.bottom")}),1.0]])]});
            extrude(context, id + "F26", {"entities" : qUnion([Q0]), "operationType" : NewBodyOperationType.REMOVE, "depth" : 30 * mm, "hasSecondDirection" : true, "secondDirectionOppositeDirection" : true, "secondDirectionDepth" : 30 * mm});
        }
        {
            var Q0;
            Q0=makeQuery(id+"F22.opExtrude","CAP_FACE",FACE,{"disambiguationData":[OSD([sQuery(id+"F20.wireOp",EDGE,"E48.MirrorC")])],"isStart":true});
            var Q1;
            Q1=makeQuery(id+"F22.opExtrude","CAP_FACE",FACE,{"disambiguationData":[OSD([sQuery(id+"F20.wireOp",EDGE,"E47")])],"isStart":true});
            extrude(context, id + "F27", {"entities" : qUnion([Q0, Q1]), "operationType" : NewBodyOperationType.REMOVE, "depth" : 25 * mm});
        }
        {
            var Q0;
            Q0=makeQuery(id+"F1.opExtrude","SWEPT_EDGE",EDGE,{"disambiguationData":[OSD([sQuery(id+"F0.wireOp",EDGE,"E13.MirrorCS"),sQuery(id+"F0.wireOp",EDGE,"E14.MirrorCS")])]});
            var Q1;
            Q1=makeQuery(id+"F2.opExtrude","SWEPT_EDGE",EDGE,{"disambiguationData":[OSD([sQuery(id+"F0.wireOp",EDGE,"E14.MirrorCS"),sQuery(id+"F0.wireOp",EDGE,"E15.MirrorCS")])]});
            var Q2;
            Q2=makeQuery(id+"F2.opExtrude","SWEPT_EDGE",EDGE,{"disambiguationData":[OSD([sQuery(id+"F0.wireOp",EDGE,"E12.bottom"),sQuery(id+"F0.wireOp",EDGE,"E12.left")])]});
            var Q3;
            Q3=makeQuery(id+"F1.opExtrude","SWEPT_EDGE",EDGE,{"disambiguationData":[OSD([sQuery(id+"F0.wireOp",EDGE,"E12.top"),sQuery(id+"F0.wireOp",EDGE,"E12.left")])]});
            fillet(context, id + "F28", {"entities" : qUnion([Q0, Q1, Q2, Q3]), "radius" : 3 * mm, "tangentPropagation" : true, "allowEdgeOverflow" : false});
        }
        {
            var Q0;
            Q0=makeQuery(id+"F3.imprint","IMPRINT",FACE,{"disambiguationData":[TD([[makeQuery(id+"F3.imprint","IMPRINT",EDGE,{"derivedFrom":sQuery(id+"F3.wireOp",EDGE,"E17")}),-1.0]])]});
            var Q1;
            Q1=makeQuery(id+"F3.imprint","IMPRINT",FACE,{"disambiguationData":[TD([[makeQuery(id+"F3.imprint","IMPRINT",EDGE,{"derivedFrom":sQuery(id+"F3.wireOp",EDGE,"E22.MirrorC")}),1.0]])]});
            var Q2;
            Q2=makeQuery(id+"F3.imprint","IMPRINT",FACE,{"disambiguationData":[TD([[makeQuery(id+"F3.imprint","IMPRINT",EDGE,{"derivedFrom":sQuery(id+"F3.wireOp",EDGE,"E30.MirrorCS")}),1.0]])]});
            var Q3;
            Q3=makeQuery(id+"F3.imprint","IMPRINT",FACE,{"disambiguationData":[TD([[makeQuery(id+"F3.imprint","IMPRINT",EDGE,{"derivedFrom":sQuery(id+"F3.wireOp",EDGE,"E18")}),-1.0]])]});
            extrude(context, id + "F29", {"entities" : qUnion([Q0, Q1, Q2, Q3]), "operationType" : NewBodyOperationType.REMOVE, "oppositeDirection" : true, "depth" : 25 * mm, "hasSecondDirection" : true, "secondDirectionOppositeDirection" : true, "secondDirectionDepth" : 2.5 * mm});
        }
    });
